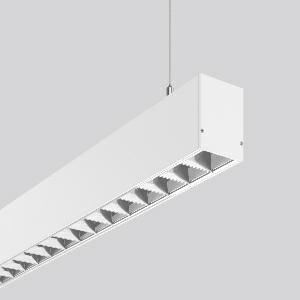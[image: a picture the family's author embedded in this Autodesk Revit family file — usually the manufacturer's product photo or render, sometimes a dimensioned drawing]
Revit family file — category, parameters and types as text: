
# Revit family: less_is_more_50_312335_002_1_a5a2
name_source: partatom
category: Lighting Fixtures
units: mm (PartAtom-declared; Revit-internal decimal feet)

## family parameters
Cut with Voids When Loaded = No
Host = Face
Light Source = No
Part Type = Normal
Room Calculation Point = No
Round Connector Dimension = Use Diameter
Shared = No

## types (1)
- LESS IS MORE 50 (1 x LED Modul 840, 2650 lm, 4000)
    Apparent Load = 22 VA
    CIE Flux Codes = 95 100 100 100 100
    Color Rendering = 80
    Color Temperature = 4000
    Default Elevation = 1800 mm
    Description = Series: LESS IS MORE 50
Linear pendant luminaire for aesthetically sophisticated lighting. Housing: extruded aluminium profile, powder-coated. End cap aluminium powder-coated. Canopy made of aluminium, powder-coated. Alea optical system: Reflector structure (ABS, Aluminium-coated, highly polished) with integrated diffuser made of non-yellowing plastic (PMMA) opal for glare-free light at the workstation (screen-compliant according to EN 12464-1). Direct light emission. Suitable for pendant. 2-point steel cable suspension freely positionable and infinitely height-adjustable. Special lengths available on request. LED unit with integrated converter interchangeable and removable. Suitable for through-wiring. With sensors or as a safety luminaire on request. 
Colour: traffic white, matt (RAL 9016)
Length: 847 mm
Width: 57 mm
Height: 75 mm
Suspension length: 2000 mm
Lamp: LED
Socket: without socket
Colour temperature: 4000K
Colour rendering index (CRI): 80
System power: 22 W
Rated luminous flux: 2650 lm
Luminous efficiency: 120 lm/W
Control gear: Regulated power supply
Protection class: I
Type of protection: IP 20
    Height = 75 mm
    Lamp = 1 x LED Modul 840
    Lamp Light Flux = 2650 lm
    Lamp count = 1
    Length = 847 mm
    Lifetime = 50000 h
    Luminous efficacy = 120 lm/W
    Manufacturer = RZB
    ModVariant = No
    Model = 312335.002.1
    Mounting Place = Ceiling
    Mounting Type = Pendant
    Number of Poles = 1
    OnlyDefault = Yes
    Power Factor = 1
    Product Name = LESS IS MORE 50
    Product group = Pendant LED linear luminaires
    ProductGroupID = 907
    Protection Class = Protection class I
    Protection Degree = IP 20
    RLX_Detail_Level = 1
    RLX_Emergency_Light_Flux = 0 lm
    RLX_Emergency_Type = 0
    RLX_Emergency_Type_DB = No
    RlxData = <blob elided: 33165 chars, md5=b481955e>
    Socket = socket
    Standby Power = 0 W
    System Light Flux = 2650 lm
    System Power = 22 W
    Type Comments = Product without accessories
    Type Image = 312342.002.jpg
    URL = http://relux.com
    VarID = ---
    Voltage = 230 V
    Voltage Range = 220-240 V
    Weight = 0.00 kg
    Width = 57 mm

## geometry (parser evidence)
native form markers: Blend x4, Sweep x10
no freeform markers — native parametric forms only
